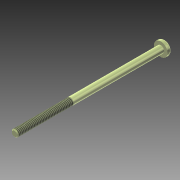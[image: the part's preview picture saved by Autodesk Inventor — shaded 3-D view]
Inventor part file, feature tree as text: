
AUTODESK INVENTOR PART (.ipt)
format: ipt  version: 2011 (Build 150239000, 239)  size: 95,232 bytes
history: native  units: mm
features: imported_body x1, thread x1
ambient origin geometry x8: Origin, YZ Plane, XZ Plane, XY Plane, X Axis, Y Axis, Z Axis, Center Point
bodies: Solid1 (feature_tree)
feature tree (2):
  imported_body  "Base1"
  thread  "Thread1"  [1 undecoded]
note: 1 required parameter value undecoded (feature->parameter linkage not recoverable at this tier; creation-order binding heuristic only, values carry confidence <= 0.55)
